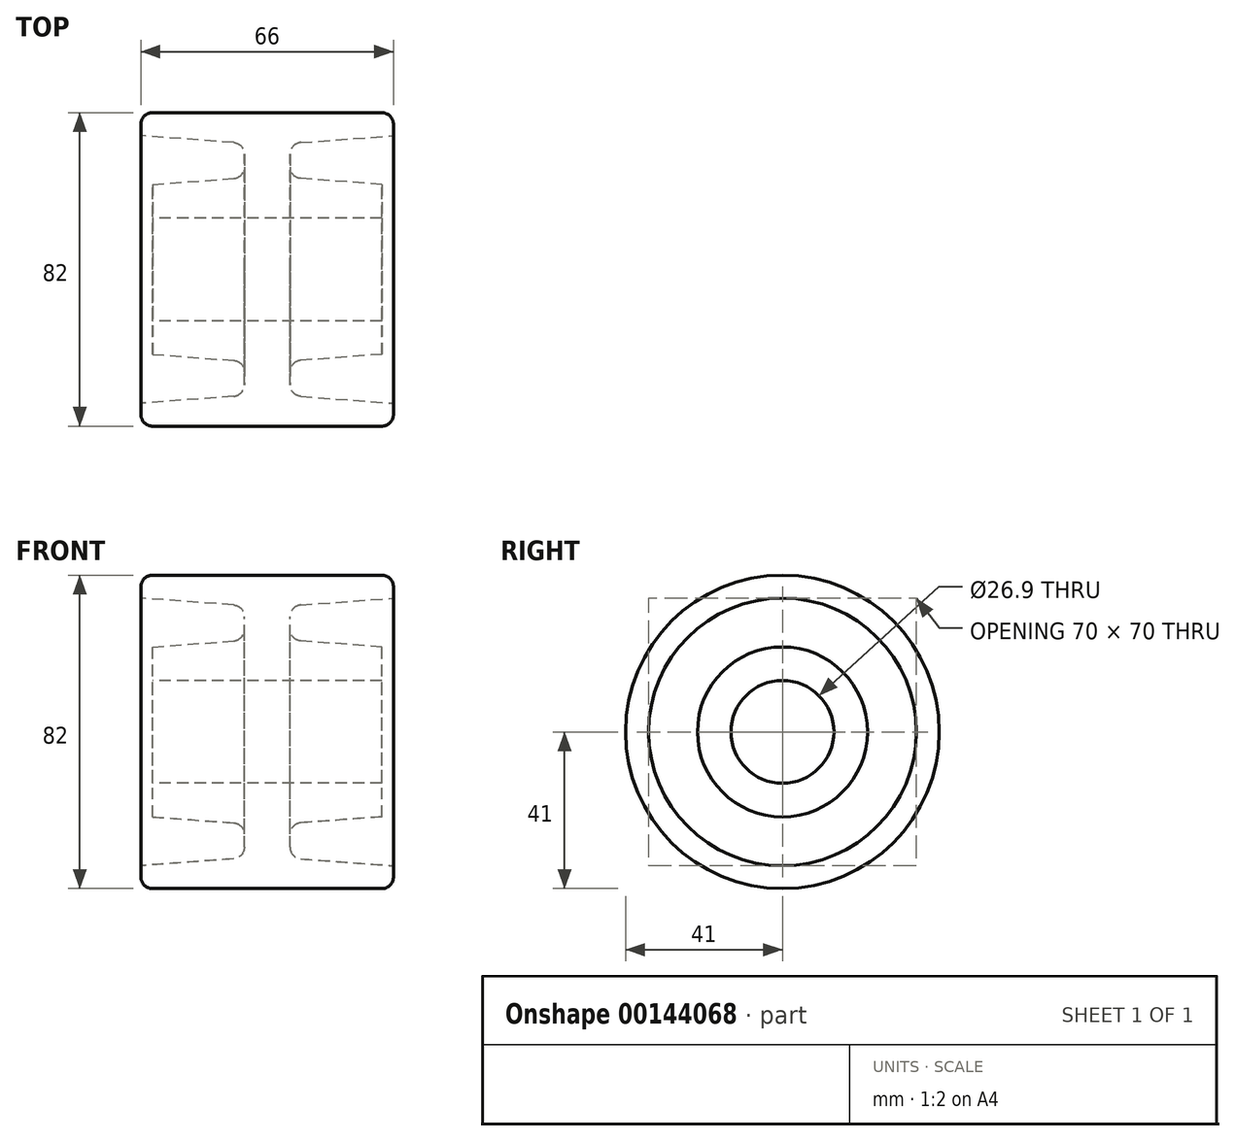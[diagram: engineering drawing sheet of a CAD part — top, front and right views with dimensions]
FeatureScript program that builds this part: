
annotation { "Feature Type Name" : "Feature", "Feature Type Description" : "" }
export const myFeature = defineFeature(function(context is Context, id is Id, definition is map)
    precondition{}
    {
        {
            var Q0;
            Q0=qCreatedBy(makeId("Right.planeOp"),FACE);
            var sketch = newSketch(context, id + "F0", { "sketchPlane" : qUnion([Q0])});
            skCircle(sketch, "E0", {"center": v(0, 0) * mm, "radius": 41 * mm});
            skCircle(sketch, "E1", {"center": v(0, 0) * mm, "radius": 13.45 * mm});
            skSolve(sketch);
        }
        {
            var Q0;
            Q0=qCreatedBy(makeId("Right.planeOp"),FACE);
            cPlane(context, id + "F1", {"entities" : qUnion([Q0]), "cplaneType" : CPlaneType.OFFSET, "offset" : 33 * mm, "width" : 150 * mm, "height" : 150 * mm});
        }
        {
            var Q0;
            Q0=qCreatedBy(id+"F1.planeOp",FACE);
            var sketch = newSketch(context, id + "F2", { "sketchPlane" : qUnion([Q0])});
            skCircle(sketch, "E2", {"center": v(0, 0) * mm, "radius": 35 * mm});
            skCircle(sketch, "E3", {"center": v(0, 0) * mm, "radius": 22 * mm});
            skSolve(sketch);
        }
        {
            var Q0;
            Q0=qCreatedBy(makeId("Right.planeOp"),FACE);
            cPlane(context, id + "F3", {"entities" : qUnion([Q0]), "cplaneType" : CPlaneType.OFFSET, "offset" : 6 * mm, "width" : 150 * mm, "height" : 150 * mm});
        }
        {
            var Q0;
            Q0=qCreatedBy(id+"F3.planeOp",FACE);
            var sketch = newSketch(context, id + "F4", { "sketchPlane" : qUnion([Q0])});
            skCircle(sketch, "E4", {"center": v(0, 0) * mm, "radius": 33 * mm});
            skCircle(sketch, "E5", {"center": v(0, 0) * mm, "radius": 24 * mm});
            skSolve(sketch);
        }
        {
            var Q0;
            Q0=qCreatedBy(makeId("Front.planeOp"),FACE);
            var sketch = newSketch(context, id + "F5", { "sketchPlane" : qUnion([Q0])});
            skLineSegment(sketch, "E6", {"start": v(33, 35) * mm, "end": v(6, 33) * mm});
            skLineSegment(sketch, "E7", {"start": v(33, 22) * mm, "end": v(6, 24) * mm});
            skLineSegment(sketch, "E8", {"start": v(33, -22) * mm, "end": v(6, -24) * mm});
            skLineSegment(sketch, "E9", {"start": v(33, -35) * mm, "end": v(6, -33) * mm});
            skLineSegment(sketch, "E10", {"start": v(33, 35) * mm, "end": v(33, 22) * mm});
            skLineSegment(sketch, "E11", {"start": v(6, 33) * mm, "end": v(6, 24) * mm});
            skLineSegment(sketch, "E12", {"start": v(56.27, 0) * mm, "end": v(-25.28, 0) * mm, "construction": true});
            skSolve(sketch);
        }
        {
            var Q0;
            Q0=makeQuery(id+"F0.imprint","IMPRINT",FACE,{"disambiguationData":[TD([[makeQuery(id+"F0.imprint","IMPRINT",EDGE,{"derivedFrom":sQuery(id+"F0.wireOp",EDGE,"E0")}),1.0]])]});
            extrude(context, id + "F6", {"entities" : qUnion([Q0]), "depth" : 33 * mm});
        }
        {
            var Q0;
            Q0=makeQuery(id+"F5.imprint","IMPRINT",FACE,{"disambiguationData":[TD([[makeQuery(id+"F5.imprint","IMPRINT",EDGE,{"derivedFrom":sQuery(id+"F5.wireOp",EDGE,"E6")}),1.0]])]});
            var Q1;
            Q1=sQuery(id+"F5.wireOp",EDGE,"E12");
            revolve(context, id + "F7", {"operationType" : NewBodyOperationType.REMOVE, "entities" : qUnion([Q0]), "axis" : qUnion([Q1]), "revolveType" : RevolveType.FULL, "oppositeDirection" : true});
        }
        {
            var Q0;
            Q0=makeQuery(id+"F7.boolean.opBoolean","COPY",EDGE,{"derivedFrom":makeQuery(id+"F7.opRevolve","SWEPT_EDGE",EDGE,{"disambiguationData":[OSD([sQuery(id+"F5.wireOp",EDGE,"E6"),sQuery(id+"F5.wireOp",EDGE,"E10")])]})});
            var Q1;
            Q1=makeQuery(id+"F6.opExtrude","CAP_EDGE",EDGE,{"disambiguationData":[OSD([sQuery(id+"F0.wireOp",EDGE,"E0")])],"isStart":false});
            var Q2;
            Q2=makeQuery(id+"F7.boolean.opBoolean","COPY",EDGE,{"derivedFrom":makeQuery(id+"F7.opRevolve","SWEPT_EDGE",EDGE,{"disambiguationData":[OSD([sQuery(id+"F5.wireOp",EDGE,"E6"),sQuery(id+"F5.wireOp",EDGE,"E11")])]})});
            var Q3;
            Q3=makeQuery(id+"F7.boolean.opBoolean","COPY",EDGE,{"derivedFrom":makeQuery(id+"F7.opRevolve","SWEPT_EDGE",EDGE,{"disambiguationData":[OSD([sQuery(id+"F5.wireOp",EDGE,"E7"),sQuery(id+"F5.wireOp",EDGE,"E11")])]})});
            fillet(context, id + "F8", {"entities" : qUnion([Q0, Q1, Q2, Q3]), "radius" : 3 * mm, "tangentPropagation" : true, "allowEdgeOverflow" : false});
        }
        {
            var Q0;
            {var subQ0=sQuery(id+"F0.wireOp",EDGE,"E1");Q0=makeQuery(id+"F7.boolean.opBoolean","SPLIT",FACE,{"disambiguationData":[TD([makeQuery(id+"F6.opExtrude","SWEPT_FACE",FACE,{"disambiguationData":[OSD([subQ0])]})])],"derivedFrom":makeQuery(id+"F6.opExtrude","CAP_FACE",FACE,{"disambiguationData":[OSD([sQuery(id+"F0.wireOp",EDGE,"E0"),subQ0])],"isStart":false})});}
            cPlane(context, id + "F9", {"entities" : qUnion([Q0]), "cplaneType" : CPlaneType.OFFSET, "offset" : 3 * mm, "oppositeDirection" : true, "width" : 150 * mm, "height" : 150 * mm});
        }
        {
            var Q0;
            Q0=qCreatedBy(id+"F9.planeOp",FACE);
            var sketch = newSketch(context, id + "F10", { "sketchPlane" : qUnion([Q0])});
            skCircle(sketch, "E13.0", {"center": v(0, 0) * mm, "radius": 23.8 * mm});
            skSolve(sketch);
        }
        {
            var Q0;
            Q0=makeQuery(id+"F10.imprint","IMPRINT",FACE,{"disambiguationData":[TD([[makeQuery(id+"F10.imprint","IMPRINT",EDGE,{"derivedFrom":sQuery(id+"F10.wireOp",EDGE,"E13.0")}),1.0]])]});
            extrude(context, id + "F11", {"entities" : qUnion([Q0]), "operationType" : NewBodyOperationType.REMOVE, "endBound" : BoundingType.THROUGH_ALL, "depth" : 25 * mm});
        }
        {
            var Q0;
            Q0=makeQuery(id+"F6.opExtrude","SWEPT_BODY",BODY,{"disambiguationData":[OSD([sQuery(id+"F0.wireOp",EDGE,"E0"),sQuery(id+"F0.wireOp",EDGE,"E1")])]});
            var Q1;
            Q1=qCreatedBy(makeId("Right.planeOp"),FACE);
            mirror(context, id + "F12", {"operationType" : NewBodyOperationType.ADD, "entities" : qUnion([Q0]), "mirrorPlane" : qUnion([Q1])});
        }
    });
